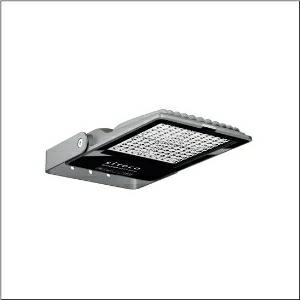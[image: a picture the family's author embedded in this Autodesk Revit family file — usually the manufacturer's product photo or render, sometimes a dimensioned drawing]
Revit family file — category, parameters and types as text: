
# Revit family: sicompact_r__31_mini___pl32_5xa7571b2k23_8fae
name_source: partatom
category: Lighting Fixtures
units: mm (PartAtom-declared; Revit-internal decimal feet)

## family parameters
Cut with Voids When Loaded = No
Host = Face
Light Source = No
Part Type = Normal
Room Calculation Point = No
Round Connector Dimension = Use Diameter
Shared = No

## types (1)
- SiCompact® 31 mini  PL32 (1 x LED, 8000 lm, 47 W, 4000K)
    Apparent Load = 47 VA
    CIE Flux Codes = 32 69 98 100 100
    Color Rendering = 70
    Color Temperature = 4000K
    Default Elevation = 1800 mm
    Description = SiCompact® 31 mini, floodlight, primary light control with lens, of plastic, of toughened safety glass, transparent, light distribution: PL32, light emission: direct distribution, primary light characteristic: asymmetric, installation type: surface-mounted, LED, High Power LED, rated luminous flux: 8.000lm, luminous efficacy: 170lm/W, light colour: 740, colour temperature: 4000K, control gear: ECG, with cable, 3x 1.5mm², mains connection: 220..240V, AC, 50/60Hz, connection cable pre-assembled, cable length: 2m, rated input power: 47W, of diecast aluminium, specular, metallic grey (RAL 9006), length: 461mm, width: 261mm, height: 62mm, bracket, of sheet steel, coated, metallic grey (RAL 9006), ON/OFF, protection rating (complete): IP66, insulation class (complete): insulation class I (protective earthing), certification: CE, impact resistance: IK08, permissible operating ambient temperature: -40..+45°C, packaging unit: 1 piece

Light Distribution: PL32
    Height = 62 mm  [stored 0.203412 ft]
    Lamp = 1 x LED
    Lamp Light Flux = 8000 lm
    Lamp Power = 47 W
    Lamp count = 1
    Length = 460 mm
    Luminous efficacy = 170 lm/W
    Manufacturer = Siteco
    ModVariant = No
    Model = 5XA7571B2K23
    Number of Poles = 1
    OnlyDefault = Yes
    Power Factor = 1
    Product Name = SiCompact® 31 mini | PL32
    Product group = floodlight | pylon top
    ProductGroupID = 6101
    Protection Class = Protection class I
    Protection Degree = IP 66
    RLX_Detail_Level = 1
    RlxData = <blob elided: 126581 chars, md5=2434ce41>
    Socket = socket
    Standby Power = 0 W
    System Light Flux = 8000 lm
    System Power = 47 W
    Type Comments = Product without accessories
    Type Image = l_1006951.jpg
    URL = http://relux.com
    VarID = ---
    Voltage = 0 V
    Weight = 0.00 kg
    Width = 260 mm

note: [stored X ft] marks values corroborated as IEEE doubles in the binary element streams (Revit-internal decimal feet)

## geometry (parser evidence)
native form markers: Blend x4, Sweep x13
no freeform markers — native parametric forms only
